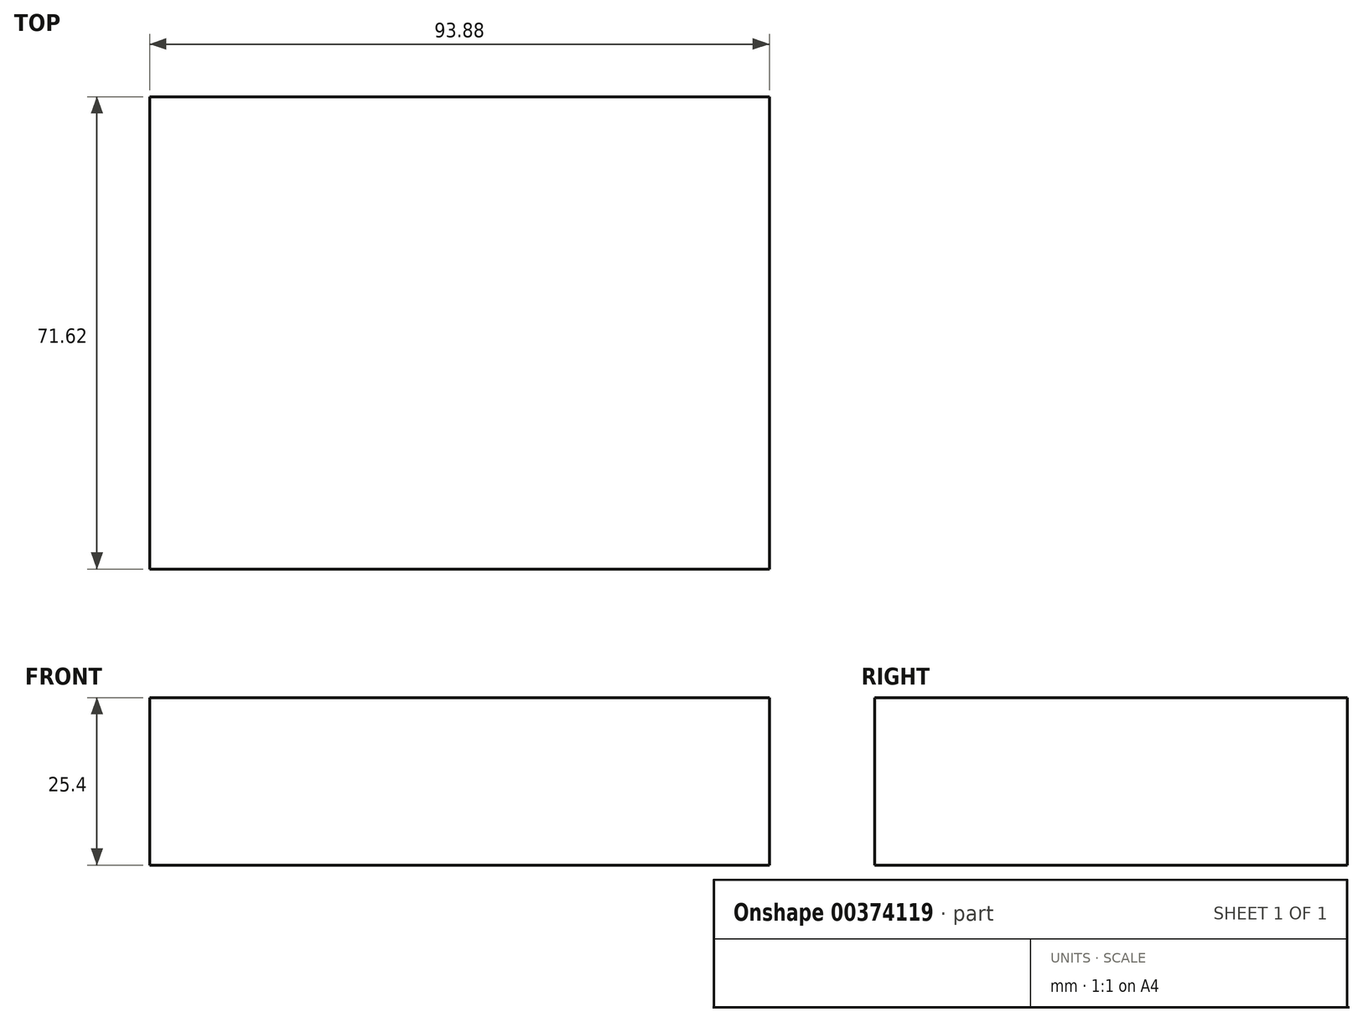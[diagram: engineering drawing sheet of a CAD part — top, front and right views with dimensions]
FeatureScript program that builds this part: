
annotation { "Feature Type Name" : "Feature", "Feature Type Description" : "" }
export const myFeature = defineFeature(function(context is Context, id is Id, definition is map)
    precondition{}
    {
        {
            var Q0;
            Q0=qCreatedBy(makeId("Top.planeOp"),FACE);
            var sketch = newSketch(context, id + "F0", { "sketchPlane" : qUnion([Q0])});
            skLineSegment(sketch, "E0.bottom", {"start": v(-46.94, -35.81) * mm, "end": v(46.94, -35.81) * mm});
            skLineSegment(sketch, "E0.top", {"start": v(-46.94, 35.81) * mm, "end": v(46.94, 35.81) * mm});
            skLineSegment(sketch, "E0.left", {"start": v(-46.94, -35.81) * mm, "end": v(-46.94, 35.81) * mm});
            skLineSegment(sketch, "E0.right", {"start": v(46.94, -35.81) * mm, "end": v(46.94, 35.81) * mm});
            skPoint(sketch, "E0.middle", {"position": v(0, 0) * mm});
            skSolve(sketch);
        }
        {
            var Q0;
            Q0 = qSketchRegion(id + "F0", true);
            extrude(context, id + "F1", {"entities" : qUnion([Q0]), "depth" : 25.4 * mm});
        }
    });
